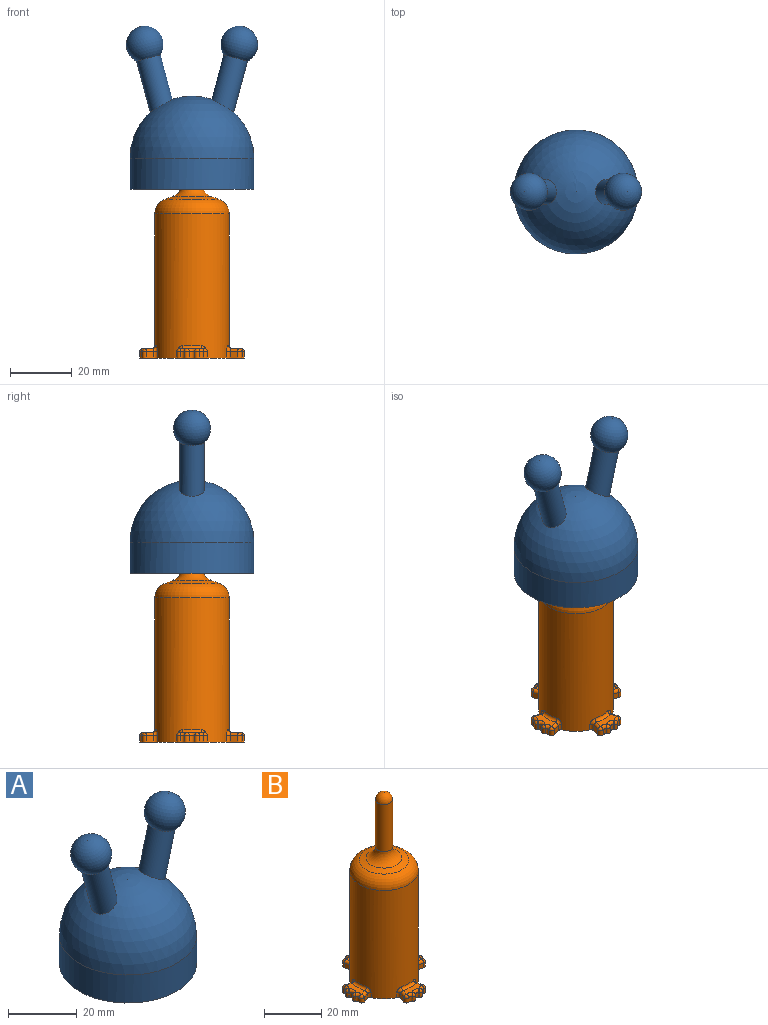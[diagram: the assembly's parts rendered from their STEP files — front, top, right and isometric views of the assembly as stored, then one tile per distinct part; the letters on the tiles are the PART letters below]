
ASSEMBLY  parts=2 mates=1
PART A: 9 faces, bbox 42.4x40x52.6 mm
  f0: sphere r=20mm, area 2408mm2, adj f4,f5,f7
  f1: sphere r=5mm, area 78.5mm2, adj f2
  f2: cone r=4.33mm half-angle=30deg, axis (0,0,-1), area 1767.1mm2, adj f1,f3
  f3: plane 40x40mm, normal (0,0,-1), area 314.2mm2, adj f2,f4
  f4: cylinder r=20mm len=40mm, axis (0,0,-1), area 1256.6mm2, adj f0,f3
  f5: cylinder r=4mm len=18.56mm, axis (0.26,0,0.97), area 401.2mm2, adj f0,f6
  f6: sphere r=6mm, area 394.8mm2, adj f5
  f7: cylinder r=4mm len=18.56mm, axis (-0.26,0,0.97), area 401.2mm2, adj f0,f8
  f8: sphere r=6mm, area 394.8mm2, adj f7
PART B: 119 faces, bbox 33.8x33.8x80 mm
  f0: plane 33.78x33.78mm, normal (0,0,-1), area 618.4mm2, adj f1,f5,f6,f7,f8,f10,f12,f15
  f1: cylinder r=12mm len=46.5mm, axis (0,0,-1), area 3358.7mm2, adj f0,f15,f19,f21,f23,f24,f43,f47
  f2: cone r=12mm half-angle=70deg, axis (0,0,-1), area 121.4mm2, adj f117,f118
  f3: cylinder r=3mm len=20.22mm, axis (0,0,-1), area 381.2mm2, adj f4,f118
  f4: sphere r=3mm, area 56.5mm2, adj f3
  f5: plane 2.46x2mm, normal (-0.31,-0.95,0), area 5.2mm2, adj f0,f22,f24,f31
  f6: plane 2.46x2mm, normal (-0.31,0.95,0), area 5.2mm2, adj f0,f15,f16,f29
  f7: plane 2x0.14mm, normal (0.62,-0.79,0), area 0.3mm2, adj f0,f11,f12,f27
  f8: plane 2x0.14mm, normal (0.62,0.79,0), area 0.3mm2, adj f0,f12,f17,f25
  f9: plane 7.89x3.28mm, normal (0,0,1), area 16.9mm2, adj f11,f13,f14,f16,f17,f20,f21,f22
  f10: cylinder r=1mm len=2mm, axis (0,0,1), area 2.6mm2, adj f0,f13,f27,f29
  f11: cylinder r=1mm len=1mm, axis (0.79,0.62,0), area 0.3mm2, adj f7,f9,f14,f28
  f12: cylinder r=1mm len=2mm, axis (0,0,-1), area 3.6mm2, adj f0,f7,f8,f14
  f13: torus R=2mm, axis (0,0,-1), area 2.8mm2, adj f9,f10,f28,f30
  f14: torus R=2mm, axis (0,0,-1), area 3.9mm2, adj f9,f11,f12,f17
  f15: cylinder r=1mm len=2mm, axis (0,0,-1), area 3mm2, adj f0,f1,f6,f19
  f16: cylinder r=1mm len=2.76mm, axis (-0.95,-0.31,0), area 4mm2, adj f6,f9,f19,f30
  f17: cylinder r=1mm len=1mm, axis (-0.79,0.62,0), area 0.3mm2, adj f8,f9,f14,f26
  f18: cylinder r=1mm len=2mm, axis (0,0,1), area 2.6mm2, adj f0,f20,f25,f31
  f19: bspline ~2.33x2.15mm, area 3.2mm2, adj f1,f15,f16,f21
  f20: torus R=2mm, axis (0,0,-1), area 2.8mm2, adj f9,f18,f26,f32
  f21: torus R=13mm, axis (0,0,-1), area 9.6mm2, adj f1,f9,f19,f23
  f22: cylinder r=1mm len=2.76mm, axis (0.95,-0.31,0), area 4mm2, adj f5,f9,f23,f32
  f23: bspline ~2.45x2.05mm, area 3.2mm2, adj f1,f21,f22,f24
  f24: cylinder r=1mm len=2mm, axis (0,0,-1), area 3mm2, adj f0,f1,f5,f23
  f25: cylinder r=1mm len=2mm, axis (0,0,1), area 3.8mm2, adj f0,f8,f18,f26
  f26: sphere r=1mm, area 1.9mm2, adj f17,f20,f25
  f27: cylinder r=1mm len=2mm, axis (0,0,1), area 3.8mm2, adj f0,f7,f10,f28
  f28: sphere r=1mm, area 1.9mm2, adj f11,f13,f27
  f29: cylinder r=1mm len=2mm, axis (0,0,1), area 4.3mm2, adj f0,f6,f10,f30
  f30: sphere r=1mm, area 2.2mm2, adj f13,f16,f29
  f31: cylinder r=1mm len=2mm, axis (0,0,1), area 4.3mm2, adj f0,f5,f18,f32
  f32: sphere r=1mm, area 2.2mm2, adj f20,f22,f31
  f33: plane 2.46x2mm, normal (-0.95,0.31,0), area 5.2mm2, adj f0,f50,f52,f59
  f34: plane 2.46x2mm, normal (0.95,0.31,0), area 5.2mm2, adj f0,f43,f44,f57
  f35: plane 2x0.14mm, normal (-0.79,-0.62,0), area 0.3mm2, adj f0,f39,f40,f55
  f36: plane 2x0.14mm, normal (0.79,-0.62,0), area 0.3mm2, adj f0,f40,f45,f53
  f37: plane 7.89x3.28mm, normal (0,0,1), area 16.9mm2, adj f39,f41,f42,f44,f45,f48,f49,f50
  f38: cylinder r=1mm len=2mm, axis (0,0,1), area 2.6mm2, adj f0,f41,f55,f57
  f39: cylinder r=1mm len=1mm, axis (0.62,-0.79,0), area 0.3mm2, adj f35,f37,f42,f56
  f40: cylinder r=1mm len=2mm, axis (0,0,-1), area 3.6mm2, adj f0,f35,f36,f42
  f41: torus R=2mm, axis (0,0,-1), area 2.8mm2, adj f37,f38,f56,f58
  f42: torus R=2mm, axis (0,0,-1), area 3.9mm2, adj f37,f39,f40,f45
  f43: cylinder r=1mm len=2mm, axis (0,0,-1), area 3mm2, adj f0,f1,f34,f47
  f44: cylinder r=1mm len=2.76mm, axis (-0.31,0.95,0), area 4mm2, adj f34,f37,f47,f58
  f45: cylinder r=1mm len=1mm, axis (0.62,0.79,0), area 0.3mm2, adj f36,f37,f42,f54
  f46: cylinder r=1mm len=2mm, axis (0,0,1), area 2.6mm2, adj f0,f48,f53,f59
  f47: bspline ~2.33x2.15mm, area 3.2mm2, adj f1,f43,f44,f49
  f48: torus R=2mm, axis (0,0,-1), area 2.8mm2, adj f37,f46,f54,f60
  f49: torus R=13mm, axis (0,0,-1), area 9.6mm2, adj f1,f37,f47,f51
  f50: cylinder r=1mm len=2.76mm, axis (-0.31,-0.95,0), area 4mm2, adj f33,f37,f51,f60
  f51: bspline ~2.45x2.05mm, area 3.2mm2, adj f1,f49,f50,f52
  f52: cylinder r=1mm len=2mm, axis (0,0,-1), area 3mm2, adj f0,f1,f33,f51
  f53: cylinder r=1mm len=2mm, axis (0,0,1), area 3.8mm2, adj f0,f36,f46,f54
  f54: sphere r=1mm, area 1.9mm2, adj f45,f48,f53
  f55: cylinder r=1mm len=2mm, axis (0,0,1), area 3.8mm2, adj f0,f35,f38,f56
  f56: sphere r=1mm, area 1.9mm2, adj f39,f41,f55
  f57: cylinder r=1mm len=2mm, axis (0,0,1), area 4.3mm2, adj f0,f34,f38,f58
  f58: sphere r=1mm, area 2.2mm2, adj f41,f44,f57
  f59: cylinder r=1mm len=2mm, axis (0,0,1), area 4.3mm2, adj f0,f33,f46,f60
  f60: sphere r=1mm, area 2.2mm2, adj f48,f50,f59
  f61: plane 2.46x2mm, normal (0.31,0.95,0), area 5.2mm2, adj f0,f78,f80,f87
  f62: plane 2.46x2mm, normal (0.31,-0.95,0), area 5.2mm2, adj f0,f71,f72,f85
  f63: plane 2x0.14mm, normal (-0.62,0.79,0), area 0.3mm2, adj f0,f67,f68,f83
  f64: plane 2x0.14mm, normal (-0.62,-0.79,0), area 0.3mm2, adj f0,f68,f73,f81
  f65: plane 7.89x3.28mm, normal (0,0,1), area 16.9mm2, adj f67,f69,f70,f72,f73,f76,f77,f78
  f66: cylinder r=1mm len=2mm, axis (0,0,1), area 2.6mm2, adj f0,f69,f83,f85
  f67: cylinder r=1mm len=1mm, axis (-0.79,-0.62,0), area 0.3mm2, adj f63,f65,f70,f84
  f68: cylinder r=1mm len=2mm, axis (0,0,-1), area 3.6mm2, adj f0,f63,f64,f70
  f69: torus R=2mm, axis (0,0,-1), area 2.8mm2, adj f65,f66,f84,f86
  f70: torus R=2mm, axis (0,0,-1), area 3.9mm2, adj f65,f67,f68,f73
  f71: cylinder r=1mm len=2mm, axis (0,0,-1), area 3mm2, adj f0,f1,f62,f75
  f72: cylinder r=1mm len=2.76mm, axis (0.95,0.31,0), area 4mm2, adj f62,f65,f75,f86
  f73: cylinder r=1mm len=1mm, axis (0.79,-0.62,0), area 0.3mm2, adj f64,f65,f70,f82
  f74: cylinder r=1mm len=2mm, axis (0,0,1), area 2.6mm2, adj f0,f76,f81,f87
  f75: bspline ~2.33x2.15mm, area 3.2mm2, adj f1,f71,f72,f77
  f76: torus R=2mm, axis (0,0,-1), area 2.8mm2, adj f65,f74,f82,f88
  f77: torus R=13mm, axis (0,0,-1), area 9.6mm2, adj f1,f65,f75,f79
  f78: cylinder r=1mm len=2.76mm, axis (-0.95,0.31,0), area 4mm2, adj f61,f65,f79,f88
  f79: bspline ~2.45x2.05mm, area 3.2mm2, adj f1,f77,f78,f80
  f80: cylinder r=1mm len=2mm, axis (0,0,-1), area 3mm2, adj f0,f1,f61,f79
  f81: cylinder r=1mm len=2mm, axis (0,0,1), area 3.8mm2, adj f0,f64,f74,f82
  f82: sphere r=1mm, area 1.9mm2, adj f73,f76,f81
  f83: cylinder r=1mm len=2mm, axis (0,0,1), area 3.8mm2, adj f0,f63,f66,f84
  f84: sphere r=1mm, area 1.9mm2, adj f67,f69,f83
  f85: cylinder r=1mm len=2mm, axis (0,0,1), area 4.3mm2, adj f0,f62,f66,f86
  f86: sphere r=1mm, area 2.2mm2, adj f69,f72,f85
  f87: cylinder r=1mm len=2mm, axis (0,0,1), area 4.3mm2, adj f0,f61,f74,f88
  f88: sphere r=1mm, area 2.2mm2, adj f76,f78,f87
  f89: plane 2.46x2mm, normal (0.95,-0.31,0), area 5.2mm2, adj f0,f106,f108,f115
  f90: plane 2.46x2mm, normal (-0.95,-0.31,0), area 5.2mm2, adj f0,f99,f100,f113
  f91: plane 2x0.14mm, normal (0.79,0.62,0), area 0.3mm2, adj f0,f95,f96,f111
  f92: plane 2x0.14mm, normal (-0.79,0.62,0), area 0.3mm2, adj f0,f96,f101,f109
  f93: plane 7.89x3.28mm, normal (0,0,1), area 16.9mm2, adj f95,f97,f98,f100,f101,f104,f105,f106
  f94: cylinder r=1mm len=2mm, axis (0,0,1), area 2.6mm2, adj f0,f97,f111,f113
  f95: cylinder r=1mm len=1mm, axis (-0.62,0.79,0), area 0.3mm2, adj f91,f93,f98,f112
  f96: cylinder r=1mm len=2mm, axis (0,0,-1), area 3.6mm2, adj f0,f91,f92,f98
  f97: torus R=2mm, axis (0,0,-1), area 2.8mm2, adj f93,f94,f112,f114
  f98: torus R=2mm, axis (0,0,-1), area 3.9mm2, adj f93,f95,f96,f101
  f99: cylinder r=1mm len=2mm, axis (0,0,-1), area 3mm2, adj f0,f1,f90,f103
  f100: cylinder r=1mm len=2.76mm, axis (0.31,-0.95,0), area 4mm2, adj f90,f93,f103,f114
  f101: cylinder r=1mm len=1mm, axis (-0.62,-0.79,0), area 0.3mm2, adj f92,f93,f98,f110
  f102: cylinder r=1mm len=2mm, axis (0,0,1), area 2.6mm2, adj f0,f104,f109,f115
  f103: bspline ~2.33x2.15mm, area 3.2mm2, adj f1,f99,f100,f105
  f104: torus R=2mm, axis (0,0,-1), area 2.8mm2, adj f93,f102,f110,f116
  f105: torus R=13mm, axis (0,0,-1), area 9.6mm2, adj f1,f93,f103,f107
  f106: cylinder r=1mm len=2.76mm, axis (0.31,0.95,0), area 4mm2, adj f89,f93,f107,f116
  f107: bspline ~2.45x2.05mm, area 3.2mm2, adj f1,f105,f106,f108
  f108: cylinder r=1mm len=2mm, axis (0,0,-1), area 3mm2, adj f0,f1,f89,f107
  f109: cylinder r=1mm len=2mm, axis (0,0,1), area 3.8mm2, adj f0,f92,f102,f110
  f110: sphere r=1mm, area 1.9mm2, adj f101,f104,f109
  f111: cylinder r=1mm len=2mm, axis (0,0,1), area 3.8mm2, adj f0,f91,f94,f112
  f112: sphere r=1mm, area 1.9mm2, adj f95,f97,f111
  f113: cylinder r=1mm len=2mm, axis (0,0,1), area 4.3mm2, adj f0,f90,f94,f114
  f114: sphere r=1mm, area 2.2mm2, adj f97,f100,f113
  f115: cylinder r=1mm len=2mm, axis (0,0,1), area 4.3mm2, adj f0,f89,f102,f116
  f116: sphere r=1mm, area 2.2mm2, adj f104,f106,f115
  f117: torus R=7mm, axis (0,0,1), area 416.3mm2, adj f1,f2
  f118: torus R=8mm, axis (0,0,-1), area 159.4mm2, adj f2,f3
PLACE A t=(-42.6,-12.82,25.36)mm
PLACE B t=(-42.6,-12.82,-29.14)mm
MATE fastened B.f1 <-> A.f2  axis (0,0,1) through (-42.6,-12.82,47.86)mm
